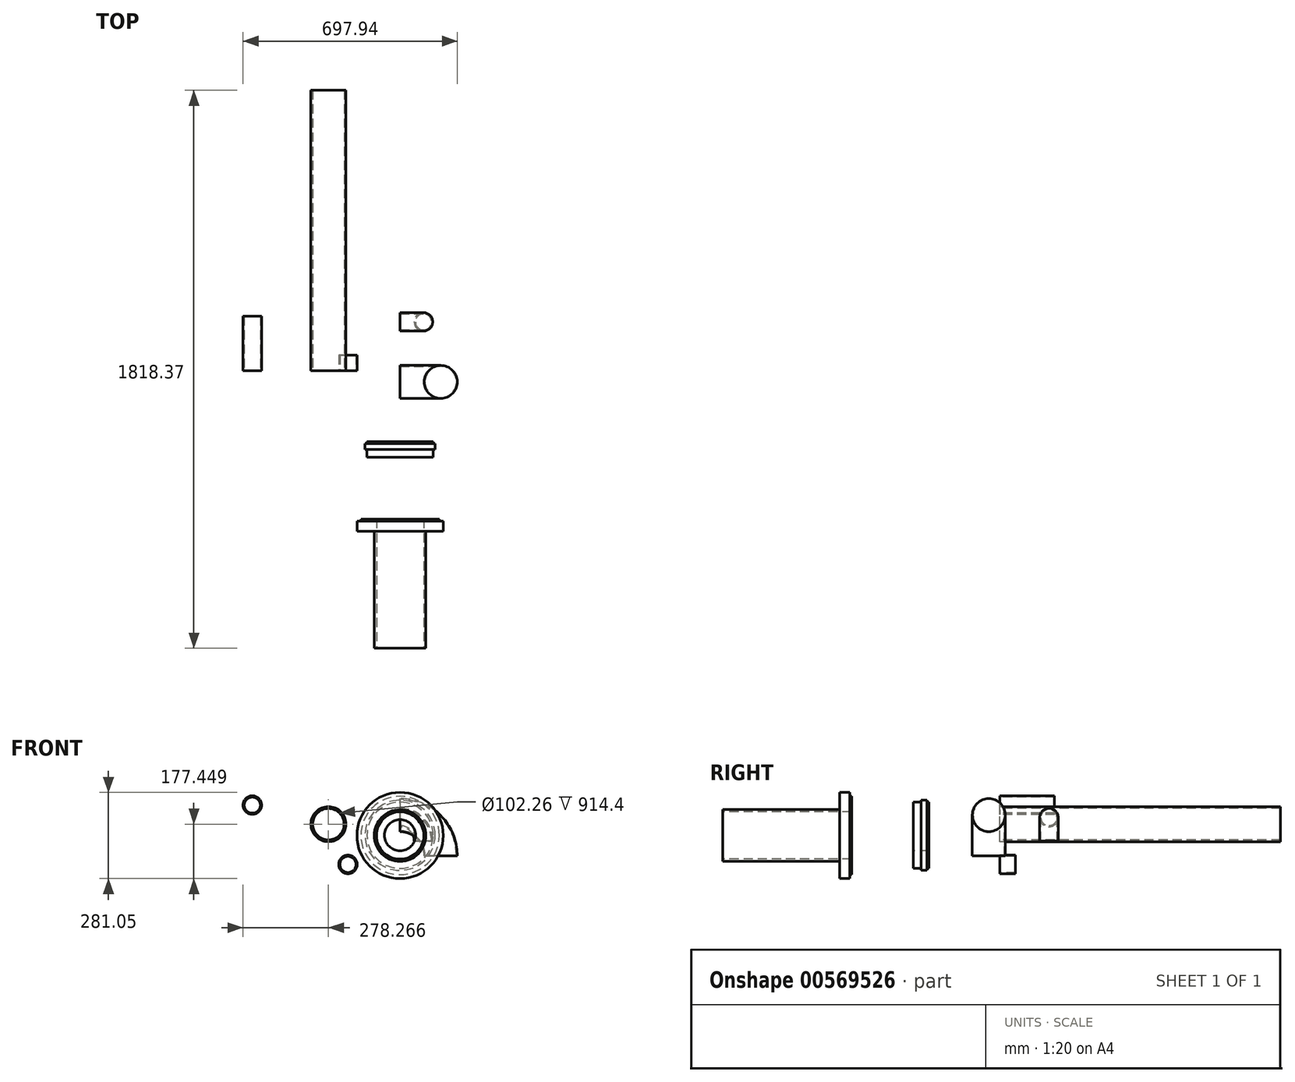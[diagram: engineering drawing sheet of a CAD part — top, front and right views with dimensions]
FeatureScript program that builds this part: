
annotation { "Feature Type Name" : "Feature", "Feature Type Description" : "" }
export const myFeature = defineFeature(function(context is Context, id is Id, definition is map)
    precondition{}
    {
        {
            var Q0;
            Q0=qCreatedBy(makeId("Right.planeOp"),FACE);
            var sketch = newSketch(context, id + "F0", { "sketchPlane" : qUnion([Q0])});
            skCircle(sketch, "E0", {"center": v(-36.26, 42.94) * mm, "radius": 53.8 * mm});
            skCircle(sketch, "E1", {"center": v(-36.26, 42.94) * mm, "radius": 51.13 * mm});
            skLineSegment(sketch, "E2", {"start": v(-229.45, -89.54) * mm, "end": v(171.14, -89.54) * mm, "construction": true});
            skSolve(sketch);
        }
        {
            var Q0;
            Q0=makeQuery(id+"F0.imprint","IMPRINT",FACE,{"disambiguationData":[TD([[makeQuery(id+"F0.imprint","IMPRINT",EDGE,{"derivedFrom":sQuery(id+"F0.wireOp",EDGE,"E0")}),1.0]])]});
            var Q1;
            Q1=sQuery(id+"F0.wireOp",EDGE,"E2");
            revolve(context, id + "F1", {"surfaceOperationType" : NewSurfaceOperationType.NEW, "entities" : qUnion([Q0]), "axis" : qUnion([Q1]), "revolveType" : RevolveType.ONE_DIRECTION, "angle" : 90 * degree});
        }
        {
            var Q0;
            Q0=qCreatedBy(makeId("Right.planeOp"),FACE);
            var sketch = newSketch(context, id + "F2", { "sketchPlane" : qUnion([Q0])});
            skCircle(sketch, "E3", {"center": v(159.55, 34.94) * mm, "radius": 30.16 * mm});
            skCircle(sketch, "E4", {"center": v(159.55, 34.94) * mm, "radius": 26.25 * mm});
            skLineSegment(sketch, "E5", {"start": v(107.11, -41.26) * mm, "end": v(219.3, -41.26) * mm});
            skSolve(sketch);
        }
        {
            var Q0;
            Q0=makeQuery(id+"F2.imprint","IMPRINT",FACE,{"disambiguationData":[TD([[makeQuery(id+"F2.imprint","IMPRINT",EDGE,{"derivedFrom":sQuery(id+"F2.wireOp",EDGE,"E3")}),1.0]])]});
            var Q1;
            Q1=sQuery(id+"F2.wireOp",EDGE,"E5");
            revolve(context, id + "F3", {"surfaceOperationType" : NewSurfaceOperationType.NEW, "entities" : qUnion([Q0]), "axis" : qUnion([Q1]), "revolveType" : RevolveType.ONE_DIRECTION, "angle" : 90 * degree});
        }
        {
            var Q0;
            Q0=qCreatedBy(makeId("Front.planeOp"),FACE);
            var sketch = newSketch(context, id + "F4", { "sketchPlane" : qUnion([Q0])});
            skCircle(sketch, "E6", {"center": v(-233.4, 13.48) * mm, "radius": 57.15 * mm});
            skCircle(sketch, "E7", {"center": v(-233.4, 13.48) * mm, "radius": 51.13 * mm});
            skSolve(sketch);
        }
        {
            var Q0;
            Q0=makeQuery(id+"F4.imprint","IMPRINT",FACE,{"disambiguationData":[TD([[makeQuery(id+"F4.imprint","IMPRINT",EDGE,{"derivedFrom":sQuery(id+"F4.wireOp",EDGE,"E6")}),1.0]])]});
            extrude(context, id + "F5", {"entities" : qUnion([Q0]), "oppositeDirection" : true, "depth" : 914.4 * mm, "offsetDistance" : 25.4 * mm});
        }
        {
            var Q0;
            Q0=qCreatedBy(makeId("Front.planeOp"),FACE);
            var sketch = newSketch(context, id + "F6", { "sketchPlane" : qUnion([Q0])});
            skCircle(sketch, "E8", {"center": v(-169.92, -117.9) * mm, "radius": 30.16 * mm});
            skCircle(sketch, "E9", {"center": v(-169.92, -117.9) * mm, "radius": 26.25 * mm});
            skSolve(sketch);
        }
        {
            var Q0;
            Q0=makeQuery(id+"F6.imprint","IMPRINT",FACE,{"disambiguationData":[TD([[makeQuery(id+"F6.imprint","IMPRINT",EDGE,{"derivedFrom":sQuery(id+"F6.wireOp",EDGE,"E8")}),1.0]])]});
            extrude(context, id + "F7", {"entities" : qUnion([Q0]), "oppositeDirection" : true, "depth" : 50.8 * mm, "offsetDistance" : 25.4 * mm});
        }
        {
            var Q0;
            Q0=qCreatedBy(makeId("Right.planeOp"),FACE);
            var sketch = newSketch(context, id + "F8", { "sketchPlane" : qUnion([Q0])});
            skLineSegment(sketch, "E10.bottom", {"start": v(-256.32, 91.53) * mm, "end": v(-237.27, 91.53) * mm});
            skLineSegment(sketch, "E10.top", {"start": v(-256.32, 28.03) * mm, "end": v(-237.27, 28.03) * mm});
            skLineSegment(sketch, "E10.left", {"start": v(-256.32, 91.53) * mm, "end": v(-256.32, 28.03) * mm});
            skLineSegment(sketch, "E10.right", {"start": v(-237.27, 91.53) * mm, "end": v(-237.27, 28.03) * mm});
            skLineSegment(sketch, "E11.bottom", {"start": v(-237.27, 28.03) * mm, "end": v(-230.92, 28.03) * mm});
            skLineSegment(sketch, "E11.top", {"start": v(-237.27, 85.18) * mm, "end": v(-230.92, 85.18) * mm});
            skLineSegment(sketch, "E11.left", {"start": v(-237.27, 28.03) * mm, "end": v(-237.27, 85.18) * mm});
            skLineSegment(sketch, "E11.right", {"start": v(-230.92, 28.03) * mm, "end": v(-230.92, 85.18) * mm});
            skLineSegment(sketch, "E12.bottom", {"start": v(-256.32, 28.03) * mm, "end": v(-281.72, 28.03) * mm});
            skLineSegment(sketch, "E12.top", {"start": v(-256.32, 85.18) * mm, "end": v(-281.72, 85.18) * mm});
            skLineSegment(sketch, "E12.left", {"start": v(-256.32, 28.03) * mm, "end": v(-256.32, 85.18) * mm});
            skLineSegment(sketch, "E12.right", {"start": v(-281.72, 28.03) * mm, "end": v(-281.72, 85.18) * mm});
            skLineSegment(sketch, "E13", {"start": v(-303.36, -22.77) * mm, "end": v(-187.75, -22.77) * mm, "construction": true});
            skSolve(sketch);
        }
        {
            var Q0;
            Q0=makeQuery(id+"F8.imprint","IMPRINT",FACE,{"disambiguationData":[TD([[makeQuery(id+"F8.imprint","IMPRINT",EDGE,{"derivedFrom":sQuery(id+"F8.wireOp",EDGE,"E12.bottom")}),-1.0]])]});
            var Q1;
            Q1=makeQuery(id+"F8.imprint","IMPRINT",FACE,{"disambiguationData":[TD([[makeQuery(id+"F8.imprint","IMPRINT",EDGE,{"derivedFrom":sQuery(id+"F8.wireOp",EDGE,"E11.bottom")}),1.0]])]});
            var Q2;
            Q2=makeQuery(id+"F8.imprint","IMPRINT",FACE,{"disambiguationData":[TD([[makeQuery(id+"F8.imprint","IMPRINT",EDGE,{"derivedFrom":sQuery(id+"F8.wireOp",EDGE,"E10.bottom")}),-1.0]])]});
            var Q3;
            Q3=sQuery(id+"F8.wireOp",EDGE,"E13");
            var Q4;
            Q4=sQuery(id+"F8.wireOp",EDGE,"E12.right");
            var Q5;
            Q5=sQuery(id+"F8.wireOp",EDGE,"E12.top");
            var Q6;
            Q6=sQuery(id+"F8.wireOp",EDGE,"E12.left");
            var Q7;
            Q7=sQuery(id+"F8.wireOp",EDGE,"E12.bottom");
            var Q8;
            Q8=sQuery(id+"F8.wireOp",EDGE,"E10.top");
            var Q9;
            Q9=sQuery(id+"F8.wireOp",EDGE,"E10.bottom");
            var Q10;
            Q10=sQuery(id+"F8.wireOp",EDGE,"E10.left");
            var Q11;
            Q11=sQuery(id+"F8.wireOp",EDGE,"E10.right");
            var Q12;
            Q12=sQuery(id+"F8.wireOp",EDGE,"E11.right");
            var Q13;
            Q13=sQuery(id+"F8.wireOp",EDGE,"E11.bottom");
            var Q14;
            Q14=sQuery(id+"F8.wireOp",EDGE,"E11.top");
            var Q15;
            Q15=sQuery(id+"F8.wireOp",EDGE,"E13");
            revolve(context, id + "F9", {"surfaceOperationType" : NewSurfaceOperationType.NEW, "entities" : qUnion([Q0, Q1, Q2]), "surfaceEntities" : qUnion([Q3, Q4, Q5, Q6, Q7, Q8, Q9, Q10, Q11, Q12, Q13, Q14]), "axis" : qUnion([Q15]), "revolveType" : RevolveType.FULL});
        }
        {
            var Q0;
            Q0=qCreatedBy(makeId("Front.planeOp"),FACE);
            var sketch = newSketch(context, id + "F10", { "sketchPlane" : qUnion([Q0])});
            skCircle(sketch, "E14", {"center": v(-481.5, 75.52) * mm, "radius": 30.16 * mm});
            skCircle(sketch, "E15", {"center": v(-481.5, 75.52) * mm, "radius": 26.25 * mm});
            skSolve(sketch);
        }
        {
            var Q0;
            Q0=makeQuery(id+"F10.imprint","IMPRINT",FACE,{"disambiguationData":[TD([[makeQuery(id+"F10.imprint","IMPRINT",EDGE,{"derivedFrom":sQuery(id+"F10.wireOp",EDGE,"E14")}),1.0]])]});
            var Q1;
            Q1=sQuery(id+"F10.wireOp",EDGE,"E14");
            var Q2;
            Q2=sQuery(id+"F10.wireOp",EDGE,"E15");
            extrude(context, id + "F11", {"entities" : qUnion([Q0]), "surfaceEntities" : qUnion([Q1, Q2]), "oppositeDirection" : true, "depth" : 177.8 * mm, "offsetDistance" : 25.4 * mm});
        }
        {
            var Q0;
            Q0=qCreatedBy(makeId("Right.planeOp"),FACE);
            var sketch = newSketch(context, id + "F12", { "sketchPlane" : qUnion([Q0])});
            skLineSegment(sketch, "E16.bottom", {"start": v(-508.68, 117.08) * mm, "end": v(-489.63, 117.08) * mm});
            skLineSegment(sketch, "E16.top", {"start": v(-508.68, 53.58) * mm, "end": v(-489.63, 53.58) * mm});
            skLineSegment(sketch, "E16.left", {"start": v(-508.68, 117.08) * mm, "end": v(-508.68, 53.58) * mm});
            skLineSegment(sketch, "E17.left", {"start": v(-489.63, 53.58) * mm, "end": v(-489.63, 117.08) * mm});
            skLineSegment(sketch, "E18.top", {"start": v(-508.68, 117.08) * mm, "end": v(-522.97, 117.08) * mm});
            skLineSegment(sketch, "E18.right", {"start": v(-522.97, 53.58) * mm, "end": v(-522.97, 117.08) * mm});
            skLineSegment(sketch, "E19.bottom", {"start": v(-522.97, 53.58) * mm, "end": v(-903.97, 53.58) * mm});
            skLineSegment(sketch, "E19.top", {"start": v(-522.97, 60.7) * mm, "end": v(-903.97, 60.7) * mm});
            skLineSegment(sketch, "E19.right", {"start": v(-903.97, 53.58) * mm, "end": v(-903.97, 60.7) * mm});
            skLineSegment(sketch, "E20", {"start": v(-522.97, 53.58) * mm, "end": v(-508.68, 53.58) * mm});
            skLineSegment(sketch, "E21", {"start": v(-748.9, -23.44) * mm, "end": v(-449.84, -23.44) * mm, "construction": true});
            skLineSegment(sketch, "E22.bottom", {"start": v(-489.63, 53.58) * mm, "end": v(-483.28, 53.58) * mm});
            skLineSegment(sketch, "E22.top", {"start": v(-489.63, 104.38) * mm, "end": v(-483.28, 104.38) * mm});
            skLineSegment(sketch, "E22.left", {"start": v(-489.63, 53.58) * mm, "end": v(-489.63, 104.38) * mm});
            skLineSegment(sketch, "E22.right", {"start": v(-483.28, 53.58) * mm, "end": v(-483.28, 104.38) * mm});
            skSolve(sketch);
        }
        {
            var Q0;
            Q0=makeQuery(id+"F12.imprint","IMPRINT",FACE,{"disambiguationData":[TD([[makeQuery(id+"F12.imprint","IMPRINT",EDGE,{"derivedFrom":sQuery(id+"F12.wireOp",EDGE,"E22.bottom")}),1.0]])]});
            var Q1;
            Q1=makeQuery(id+"F12.imprint","IMPRINT",FACE,{"disambiguationData":[TD([[makeQuery(id+"F12.imprint","IMPRINT",EDGE,{"derivedFrom":sQuery(id+"F12.wireOp",EDGE,"E16.bottom")}),-1.0]])]});
            var Q2;
            Q2=makeQuery(id+"F12.imprint","IMPRINT",FACE,{"disambiguationData":[TD([[makeQuery(id+"F12.imprint","IMPRINT",EDGE,{"derivedFrom":sQuery(id+"F12.wireOp",EDGE,"E16.left")}),-1.0]])]});
            var Q3;
            {var subQ0=sQuery(id+"F12.wireOp",EDGE,"E19.bottom");Q3=makeQuery(id+"F12.imprint","IMPRINT",FACE,{"disambiguationData":[TD([[makeQuery(id+"F12.imprint","IMPRINT",EDGE,{"derivedFrom":subQ0}),-1.0]])]});}
            var Q4;
            Q4=sQuery(id+"F12.wireOp",EDGE,"E21");
            revolve(context, id + "F13", {"surfaceOperationType" : NewSurfaceOperationType.NEW, "entities" : qUnion([Q0, Q1, Q2, Q3]), "axis" : qUnion([Q4]), "revolveType" : RevolveType.FULL});
        }
    });
